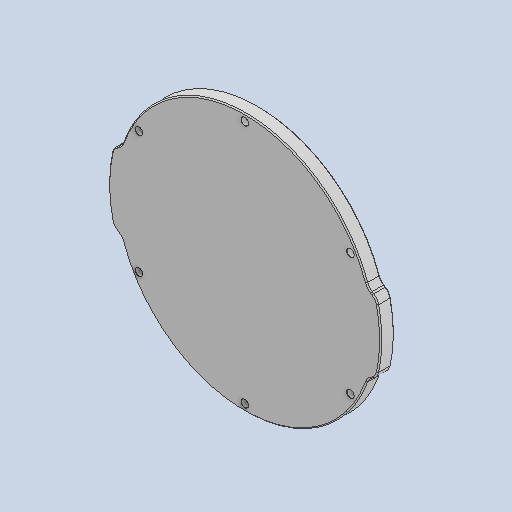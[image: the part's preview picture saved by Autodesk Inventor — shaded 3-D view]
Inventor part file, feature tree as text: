
AUTODESK INVENTOR PART (.ipt)
format: ipt  version: 2025.1 (Build 291241020, 241B)  size: 157,696 bytes
history: native  units: in
note: dims shown in document units (in); Inventor stores cm internally (conversion verified against a paired STEP export)
features: chamfer x1
ambient origin geometry x8: Origin, YZ Plane, XZ Plane, XY Plane, X Axis, Y Axis, Z Axis, Center Point
bodies: Solid1 (feature_tree)
feature tree (1):
  chamfer  "Chamfer21"  [1 undecoded]
note: 1 required parameter value undecoded (feature->parameter linkage not recoverable at this tier; creation-order binding heuristic only, values carry confidence <= 0.55)
